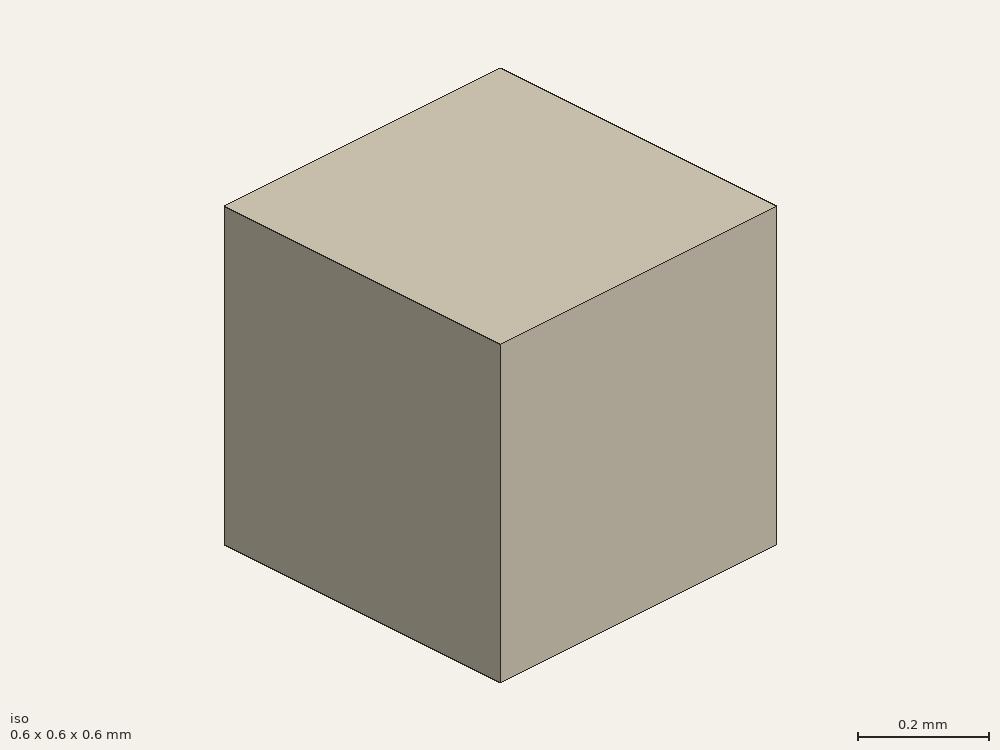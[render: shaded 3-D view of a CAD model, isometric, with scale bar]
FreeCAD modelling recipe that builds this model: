
FCSTD DOCUMENT  (FreeCAD 0.19R)
Label: test_shape
License: All rights reserved
LicenseURL: http://en.wikipedia.org/wiki/All_rights_reserved
objects: Sketcher::SketchObject×1, PartDesign::Pad×1, PartDesign::Body×1
note: 4 computed .brp shape members not serialized (recipe doc carries the construction recipe); baked Part::Feature solids carry a one-line shape summary decoded from their .brp

FEATURE [Sketcher::SketchObject] Sketch
  FullyConstrained = true
  MapMode = 5
  Support = -> [XY_Plane]
  sketch-geometry (4):
    g0: LineSegment StartX=0.3 StartY=0.3 StartZ=0 EndX=-0.3 EndY=0.3 EndZ=0
    g1: LineSegment StartX=-0.3 StartY=0.3 StartZ=0 EndX=-0.3 EndY=-0.3 EndZ=0
    g2: LineSegment StartX=-0.3 StartY=-0.3 StartZ=0 EndX=0.3 EndY=-0.3 EndZ=0
    g3: LineSegment StartX=0.3 StartY=-0.3 StartZ=0 EndX=0.3 EndY=0.3 EndZ=0
  constraints (11):
    c: Coincident(g0,g1)
    c: Coincident(g1,g2)
    c: Coincident(g2,g3)
    c: Coincident(g3,g0)
    c: Horizontal(g0)
    c: Horizontal(g2)
    c: Vertical(g1)
    c: Vertical(g3)
    c: Symmetric(g0,g1,g-1)
    c: Equal(g3,g0)
    c: DistanceY(g3,g3) = 0.6
FEATURE [PartDesign::Pad] Pad
  Direction = (1,1,1)
  Length = 0.6
  Length2 = 100
  Midplane = true
  Profile = -> Sketch
  Type = 0
FEATURE [PartDesign::Body] Body
  Group = -> [Sketch,Pad]
  Origin = -> Origin
  Tip = -> Pad
